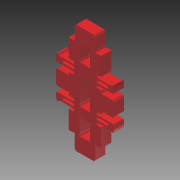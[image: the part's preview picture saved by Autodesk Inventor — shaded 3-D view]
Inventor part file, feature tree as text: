
AUTODESK INVENTOR PART (.ipt)
format: ipt  version: 2012 SP1 (Build 160190100, 190)  size: 279,552 bytes
history: native  units: in
note: dims shown in document units (in); Inventor stores cm internally (conversion verified against a paired STEP export)
features: other x3, extrude x1
ambient origin geometry x8: Origin, YZ Plane, XZ Plane, XY Plane, X Axis, Y Axis, Z Axis, Center Point
bodies: Solid1 (feature_tree)
feature tree (4):
  other  "skeleton.ipt"
  other  "STOCK_12MM"
  extrude  "Extrusion1"  Depth=0.3937in
  other  "THROUGH-CUT"
